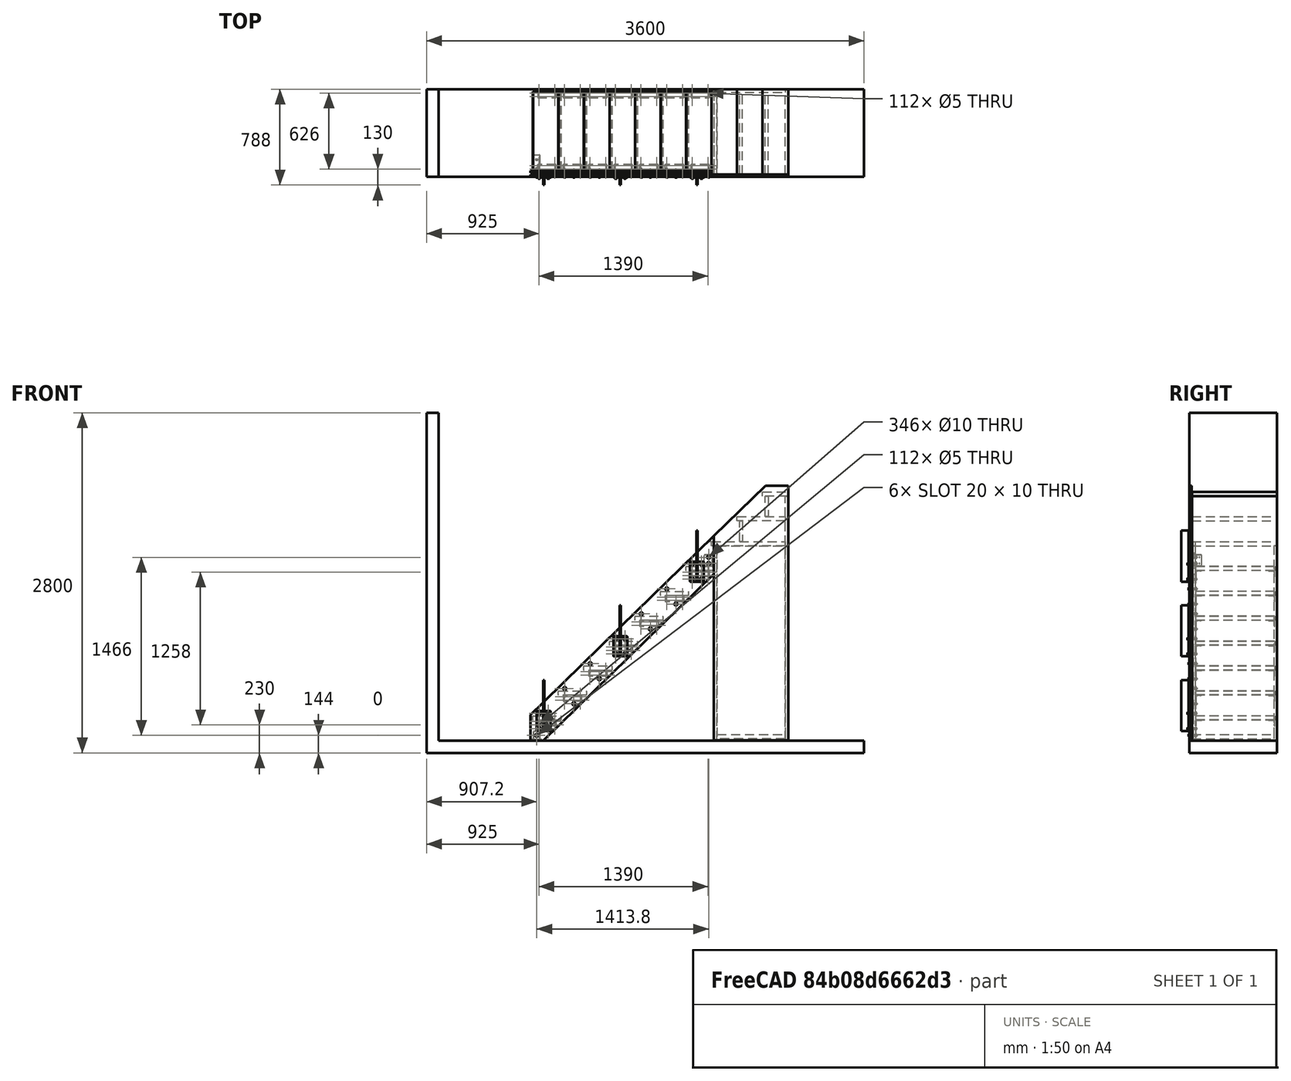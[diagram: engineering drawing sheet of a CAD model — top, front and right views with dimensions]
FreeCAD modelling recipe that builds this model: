
FCSTD DOCUMENT  (FreeCAD 0.17R10980 (Git))
Label: double_beam
License: All rights reserved
LicenseURL: http://en.wikipedia.org/wiki/All_rights_reserved
objects: Part::FeaturePython×27, Part::Part2DObjectPython×22, Part::Extrusion×12, Part::Compound×11, Part::Feature×9, Part::Cut×5, App::DocumentObjectGroupPython×2, App::DocumentObjectGroup×2
note: 86 computed .brp shape members not serialized (recipe doc carries the construction recipe); baked Part::Feature solids carry a one-line shape summary decoded from their .brp

FEATURE [Part::FeaturePython] beam_01  # a2plus imported part (geometry in sourceFile) (typed FeaturePython)
  fixedPosition = true
  sourceFile = beam.fcstd
  timeLastImport = 1.49397e+09
  updateColors = true
FEATURE [Part::FeaturePython] fridge_box_panels_01  # a2plus imported part (geometry in sourceFile) (typed FeaturePython)
  fixedPosition = false
  sourceFile = A711_fridge_box_panels.fcstd
  timeLastImport = 1.49389e+09
  updateColors = true
FEATURE [Part::Feature] fridge_box_panels_01_cs
  shape: bbox 630 x 3e-07 x 2050 mm, 0 faces, 0 solids (baked)
FEATURE [Part::Part2DObjectPython] DWire  # Draft 2D object (typed FeaturePython)
  ChamferSize = 0
  Closed = true
  End = (1515,-325,1605)
  FilletRadius = 0
  Length = 488.683
  MakeFace = true
  Points = (7) [(1490,-325,1605),(1470,-325,1605),(1470,-325,1640),(1423.45,-325,1640),(1423.45,-325,1757.79),(1515,-325,1757.79),(1515,-325,1605)]
  Start = (1490,-325,1605)
  Subdivisions = 0
  Support = -> [beam_01]
FEATURE [Part::FeaturePython] Clone  label="beam_004"  # Draft clone (typed FeaturePython)
  AttacherType = Attacher::AttachEngine3D
  Objects = -> [beam_01]
  Placement = pos=(0,-30,0) rot=(0,0,1;0rad)
  Scale = (1,1,1)
FEATURE [Part::FeaturePython] stair_profile_01  # a2plus imported part (geometry in sourceFile) (typed FeaturePython)
  fixedPosition = false
  sourceFile = stair_profile.fcstd
  timeLastImport = 1.4938e+09
  updateColors = true
FEATURE [Part::FeaturePython] step_01  # a2plus imported part (geometry in sourceFile) (typed FeaturePython)
  fixedPosition = false
  sourceFile = step.fcstd
  timeLastImport = 1.4938e+09
  updateColors = true
FEATURE [Part::FeaturePython] beam_plate_01  # a2plus imported part (geometry in sourceFile) (typed FeaturePython)
  fixedPosition = false
  sourceFile = beam_plate.fcstd
  timeLastImport = 1.49389e+09
  updateColors = true
FEATURE [Part::Feature] Union
  shape: bbox 26 x 2e-07 x 126 mm, 1 faces, 0 solids (baked)
FEATURE [Part::Feature] Union001
  shape: bbox 86 x 2e-07 x 26 mm, 1 faces, 0 solids (baked)
FEATURE [Part::Part2DObjectPython] Circle001  # Draft 2D object (typed FeaturePython)
  FirstAngle = 0
  LastAngle = 0
  MakeFace = true
  Placement = pos=(32.2,-325,44) rot=(-1,0,0;1.5708rad)
  Radius = 5
FEATURE [Part::Part2DObjectPython] Circle  # Draft 2D object (typed FeaturePython)
  FirstAngle = 0
  LastAngle = 0
  MakeFace = true
  Placement = pos=(1446,-325,1510) rot=(-1,0,0;1.5708rad)
  Radius = 5
FEATURE [Part::Part2DObjectPython] Circle002  # Draft 2D object (typed FeaturePython)
  FirstAngle = 0
  LastAngle = 0
  MakeFace = true
  Placement = pos=(1446,-325,1460) rot=(-1,0,0;1.5708rad)
  Radius = 5
FEATURE [Part::Compound] Compound001
  Links = -> [Union,Union001,DWire]
FEATURE [Part::Compound] Compound002
  Links = -> [Circle001,Circle,Circle002]
FEATURE [Part::Compound] Compound003
  Links = -> [Compound002,Compound001]
FEATURE [Part::Extrusion] Extrude
  Base = -> Compound003
  Dir = (0,-1,0)
  DirMode = 0
  FaceMakerClass = Part::FaceMakerBullseye
  LengthFwd = 20
  LengthRev = 0
  Solid = false
  Symmetric = false
FEATURE [Part::Cut] Cut
  Base = -> beam_01
  Tool = -> Extrude
FEATURE [Part::FeaturePython] Panel001  # WARN: FeaturePython — macro-defined, semantics opaque (R4)
  Area = 0
  Base = -> Cut
  FaceMaker = 0
  HorizontalArea = 0
  Length = 0
  MoveWithHost = false
  Normal = (0,0,0)
  PerimeterLength = 0
  Role = 0
  Sheets = 1
  Thickness = 10
  VerticalArea = 0
  WaveDirection = 0
  WaveHeight = 0
  WaveLength = 0
  WaveType = 0
  Width = 0
FEATURE [Part::Extrusion] Extrude001
  Base = -> Compound002
  Dir = (0,-1,0)
  DirMode = 0
  FaceMakerClass = Part::FaceMakerBullseye
  LengthFwd = 20
  LengthRev = 0
  Placement = pos=(0,-30,0) rot=(0,0,1;0rad)
  Solid = false
  Symmetric = false
FEATURE [Part::Cut] Cut001
  Base = -> Clone
  Tool = -> Extrude001
FEATURE [Part::FeaturePython] Panel  # WARN: FeaturePython — macro-defined, semantics opaque (R4)
  Area = 0
  Base = -> Cut001
  FaceMaker = 0
  HorizontalArea = 0
  Length = 0
  MoveWithHost = false
  Normal = (0,0,0)
  PerimeterLength = 0
  Role = 0
  Sheets = 1
  Thickness = 10
  VerticalArea = 0
  WaveDirection = 0
  WaveHeight = 0
  WaveLength = 0
  WaveType = 0
  Width = 0
FEATURE [Part::Part2DObjectPython] Circle003  # Draft 2D object (typed FeaturePython)
  FirstAngle = 0
  LastAngle = 0
  MakeFace = true
  Placement = pos=(32.2,-375,44) rot=(1,0,0;1.5708rad)
  Radius = 12.5
FEATURE [Part::Extrusion] Extrude002
  Base = -> Circle003
  Dir = (0,-1,0)
  DirMode = 0
  FaceMakerClass = Part::FaceMakerBullseye
  LengthFwd = 2
  LengthRev = 0
  Solid = false
  Symmetric = false
FEATURE [Part::Part2DObjectPython] Circle004  # Draft 2D object (typed FeaturePython)
  FirstAngle = 0
  LastAngle = 0
  MakeFace = true
  Placement = pos=(32.2,-375,44) rot=(1,0,0;1.5708rad)
  Radius = 5
FEATURE [Part::Extrusion] Extrude003
  Base = -> Circle004
  Dir = (0,-1,0)
  DirMode = 0
  FaceMakerClass = Part::FaceMakerBullseye
  LengthFwd = 2
  LengthRev = 0
  Solid = false
  Symmetric = false
FEATURE [Part::Cut] Cut002  label="washer"
  Base = -> Extrude002
  Tool = -> Extrude003
FEATURE [Part::Feature] BOLTS_part011_cs
  Placement = pos=(0,0,-2.5) rot=(0,0,1;0rad)
  shape: bbox 17 x 19.63 x 3e-07 mm, 0 faces, 0 solids (baked)
FEATURE [Part::Extrusion] Extrude004  label="nuts"
  Base = -> BOLTS_part011_cs
  Dir = (0,0,1)
  DirMode = 0
  FaceMakerClass = Part::FaceMakerBullseye
  LengthFwd = 6
  LengthRev = 0
  Placement = pos=(32.2,-347,44) rot=(1,0,0;1.5708rad)
  Solid = true
  Symmetric = false
FEATURE [Part::FeaturePython] Component001  label="washer002"  # WARN: FeaturePython — macro-defined, semantics opaque (R4)
  CloneOf = -> Cut002
  HorizontalArea = 0
  MoveWithHost = false
  PerimeterLength = 0
  Placement = pos=(0,30,0) rot=(0,0,1;0rad)
  Role = 0
  VerticalArea = 0
FEATURE [Part::FeaturePython] Component002  label="washer003"  # WARN: FeaturePython — macro-defined, semantics opaque (R4)
  CloneOf = -> Cut002
  HorizontalArea = 0
  MoveWithHost = false
  PerimeterLength = 0
  Placement = pos=(0,52,0) rot=(0,0,1;0rad)
  Role = 0
  VerticalArea = 0
FEATURE [Part::FeaturePython] Component003  label="nuts001"  # WARN: FeaturePython — macro-defined, semantics opaque (R4)
  CloneOf = -> Extrude004
  HorizontalArea = 0
  MoveWithHost = false
  PerimeterLength = 0
  Placement = pos=(32.2,-317,44) rot=(1,0,0;1.5708rad)
  Role = 0
  VerticalArea = 0
FEATURE [Part::Feature] BOLTS_part  label="Hexagon head bolt DIN 931 M10 - 66.0"
  Placement = pos=(32.2,-383.4,44) rot=(-1,0,0;1.5708rad)
  shape: bbox 17 x 72.4 x 19.63 mm, 11 faces (baked)
FEATURE [Part::Feature] step_01_cs  label="hd_steps_cs"
  shape: bbox 1490 x 3e-07 x 1265 mm, 0 faces, 0 solids (baked)
FEATURE [Part::FeaturePython] fridge_box_door_01  # a2plus imported part (geometry in sourceFile) (typed FeaturePython)
  Placement = pos=(0,1e-12,0) rot=(0,0,1;0rad)
  fixedPosition = false
  sourceFile = fridge_box_door.fcstd
  timeLastImport = 1.49385e+09
  updateColors = true
FEATURE [Part::Feature] fridge_box_door_01_cs
  shape: bbox 610 x 3e-07 x 2095 mm, 0 faces, 0 solids (baked)
FEATURE [Part::Part2DObjectPython] DWire003  # Draft 2D object (typed FeaturePython)
  ChamferSize = 0
  Closed = false
  End = (1490,-375,1605)
  FilletRadius = 0
  Length = 55
  MakeFace = true
  Points = (3) [(1470,-375,1640),(1470,-375,1605),(1490,-375,1605)]
  Start = (1470,-375,1640)
  Subdivisions = 0
FEATURE [Part::Part2DObjectPython] Line  # Draft 2D object (typed FeaturePython)
  ChamferSize = 0
  Closed = false
  End = (1490,-375,1640)
  FilletRadius = 0
  Length = 20
  MakeFace = true
  Points = (2) [(1470,-375,1640),(1490,-375,1640)]
  Start = (1470,-375,1640)
  Subdivisions = 0
FEATURE [Part::Part2DObjectPython] Line001  # Draft 2D object (typed FeaturePython)
  ChamferSize = 0
  Closed = false
  End = (1490,-375,0)
  FilletRadius = 0
  Length = 5
  MakeFace = true
  Points = (2) [(1490,-375,5),(1490,-375,0)]
  Start = (1490,-375,5)
  Subdivisions = 0
FEATURE [Part::Part2DObjectPython] Line002  # Draft 2D object (typed FeaturePython)
  ChamferSize = 0
  Closed = false
  End = (2100,-375,0)
  FilletRadius = 0
  Length = 5
  MakeFace = true
  Points = (2) [(2100,-375,5),(2100,-375,2.27374e-13)]
  Start = (2100,-375,5)
  Subdivisions = 0
FEATURE [Part::Part2DObjectPython] DWire001  # Draft 2D object (typed FeaturePython)
  ChamferSize = 0
  Closed = false
  End = (2725,-375,0)
  FilletRadius = 0
  Length = 6200
  MakeFace = true
  Points = (3) [(-775,-375,2700),(-775,-375,-1.13687e-13),(2725,-375,1.00626e-13)]
  Start = (-775,-375,2700)
  Subdivisions = 0
FEATURE [Part::Part2DObjectPython] DWire002  # Draft 2D object (typed FeaturePython)
  ChamferSize = 0
  Closed = false
  End = (2725,-375,2105)
  FilletRadius = 0
  Length = 1405
  MakeFace = true
  Points = (4) [(2725,-375,2260),(2100,-375,2260),(2100,-375,2105),(2725,-375,2105)]
  Start = (2725,-375,2260)
  Subdivisions = 0
FEATURE [Part::Compound] Compound007  label="07_section"
  Links = -> [DWire002,DWire001]
FEATURE [Part::FeaturePython] Component007  label="07_section002"  # WARN: FeaturePython — macro-defined, semantics opaque (R4)
  CloneOf = -> Compound007
  HorizontalArea = 0
  MoveWithHost = false
  PerimeterLength = 0
  Role = 0
  VerticalArea = 0
FEATURE [Part::FeaturePython] Component008  label="07_section003"  # WARN: FeaturePython — macro-defined, semantics opaque (R4)
  CloneOf = -> Compound007
  HorizontalArea = 0
  MoveWithHost = false
  PerimeterLength = 0
  Role = 0
  VerticalArea = 0
FEATURE [App::DocumentObjectGroupPython] VisGroup001  label="hd_steps"  # scripted group (container) (typed FeaturePython)
  Group = -> [step_01_cs,Component008]
FEATURE [Part::FeaturePython] Component009  label="07_section004"  # WARN: FeaturePython — macro-defined, semantics opaque (R4)
  CloneOf = -> Compound007
  HorizontalArea = 0
  MoveWithHost = false
  PerimeterLength = 0
  Role = 0
  VerticalArea = 0
FEATURE [Part::FeaturePython] railing_plate_01  # a2plus imported part (geometry in sourceFile) (typed FeaturePython)
  fixedPosition = false
  sourceFile = railing_plate.fcstd
  timeLastImport = 1.49397e+09
  updateColors = true
FEATURE [Part::Compound] Compound010  label="main"
  Links = -> [Panel,Panel001]
FEATURE [Part::Part2DObjectPython] Circle005  # Draft 2D object (typed FeaturePython)
  FirstAngle = 0
  LastAngle = 0
  MakeFace = true
  Placement = pos=(32.2,-375,44) rot=(1,0,0;1.5708rad)
  Radius = 12.5
FEATURE [Part::Extrusion] Extrude007
  Base = -> Circle005
  Dir = (0,-1,0)
  DirMode = 0
  FaceMakerClass = Part::FaceMakerBullseye
  LengthFwd = 2
  LengthRev = 0
  Solid = false
  Symmetric = false
FEATURE [Part::Part2DObjectPython] Circle006  # Draft 2D object (typed FeaturePython)
  FirstAngle = 0
  LastAngle = 0
  MakeFace = true
  Placement = pos=(32.2,-375,44) rot=(1,0,0;1.5708rad)
  Radius = 5
FEATURE [Part::Extrusion] Extrude008
  Base = -> Circle006
  Dir = (0,-1,0)
  DirMode = 0
  FaceMakerClass = Part::FaceMakerBullseye
  LengthFwd = 2
  LengthRev = 0
  Solid = false
  Symmetric = false
FEATURE [Part::Cut] Cut003  label="washer004"
  Base = -> Extrude007
  Placement = pos=(0,-8,0) rot=(0,0,1;0rad)
  Tool = -> Extrude008
FEATURE [Part::Feature] BOLTS_part011_cs001
  Placement = pos=(0,0,-2.5) rot=(0,0,1;0rad)
  shape: bbox 17 x 19.63 x 3e-07 mm, 0 faces, 0 solids (baked)
FEATURE [Part::Extrusion] Extrude009  label="nuts002"
  Base = -> BOLTS_part011_cs001
  Dir = (0,0,1)
  DirMode = 0
  FaceMakerClass = Part::FaceMakerBullseye
  LengthFwd = 6
  LengthRev = 0
  Placement = pos=(32.2,-347,44) rot=(1,0,0;1.5708rad)
  Solid = true
  Symmetric = false
FEATURE [Part::FeaturePython] Component011  label="washer006"  # WARN: FeaturePython — macro-defined, semantics opaque (R4)
  CloneOf = -> Cut003
  HorizontalArea = 0
  MoveWithHost = false
  PerimeterLength = 0
  Placement = pos=(0,30,0) rot=(0,0,1;0rad)
  Role = 0
  VerticalArea = 0
FEATURE [Part::FeaturePython] Component012  label="washer007"  # WARN: FeaturePython — macro-defined, semantics opaque (R4)
  CloneOf = -> Cut003
  HorizontalArea = 0
  MoveWithHost = false
  PerimeterLength = 0
  Placement = pos=(0,52,0) rot=(0,0,1;0rad)
  Role = 0
  VerticalArea = 0
FEATURE [Part::FeaturePython] Component013  label="nuts003"  # WARN: FeaturePython — macro-defined, semantics opaque (R4)
  CloneOf = -> Extrude009
  HorizontalArea = 0
  MoveWithHost = false
  PerimeterLength = 0
  Placement = pos=(32.2,-317,44) rot=(1,0,0;1.5708rad)
  Role = 0
  VerticalArea = 0
FEATURE [Part::Feature] BOLTS_part001  label="Hexagon head bolt DIN 931 M10 - 66.001"
  Placement = pos=(32.2,-391.4,44) rot=(-1,0,0;1.5708rad)
  shape: bbox 17 x 72.4 x 19.63 mm, 11 faces (baked)
FEATURE [Part::Part2DObjectPython] Circle009  # Draft 2D object (typed FeaturePython)
  FirstAngle = 0
  LastAngle = 0
  MakeFace = true
  Placement = pos=(32.2,-355,44) rot=(1,0,0;1.5708rad)
  Radius = 12.5
FEATURE [Part::Extrusion] Extrude013
  Base = -> Circle009
  Dir = (0,1,0)
  DirMode = 0
  FaceMakerClass = Part::FaceMakerBullseye
  LengthFwd = 2
  LengthRev = 0
  Solid = false
  Symmetric = false
FEATURE [Part::Part2DObjectPython] Circle010  # Draft 2D object (typed FeaturePython)
  FirstAngle = 0
  LastAngle = 0
  MakeFace = true
  Placement = pos=(32.2,-355,44) rot=(1,0,0;1.5708rad)
  Radius = 5
FEATURE [Part::Extrusion] Extrude014
  Base = -> Circle010
  Dir = (0,1,0)
  DirMode = 0
  FaceMakerClass = Part::FaceMakerBullseye
  LengthFwd = 2
  LengthRev = 0
  Solid = false
  Symmetric = false
FEATURE [Part::Cut] Cut005  label="washer012"
  Base = -> Extrude013
  Tool = -> Extrude014
FEATURE [Part::Compound] Compound004  label="fastener_and_nuts"
  Links = -> [Cut002,Extrude004,Component003,Component001,Component002,BOLTS_part,Cut005]
FEATURE [Part::FeaturePython] Component005  label="fastener_and_nuts002"  # WARN: FeaturePython — macro-defined, semantics opaque (R4)
  CloneOf = -> Compound004
  HorizontalArea = 0
  MoveWithHost = false
  PerimeterLength = 0
  Placement = pos=(1413.8,0,1466) rot=(0,0,1;0rad)
  Role = 0
  VerticalArea = 0
FEATURE [Part::FeaturePython] Component006  label="fastener_and_nuts003"  # WARN: FeaturePython — macro-defined, semantics opaque (R4)
  CloneOf = -> Compound004
  HorizontalArea = 0
  MoveWithHost = false
  PerimeterLength = 0
  Placement = pos=(1413.8,0,1416) rot=(0,0,1;0rad)
  Role = 0
  VerticalArea = 0
FEATURE [Part::Compound] Compound016  label="fasteners_and_nuts_unique"
  Links = -> [Component005,Compound004,Component006]
FEATURE [Part::FeaturePython] Component  label="washer013"  # WARN: FeaturePython — macro-defined, semantics opaque (R4)
  CloneOf = -> Cut005
  HorizontalArea = 0
  MoveWithHost = false
  PerimeterLength = 0
  Role = 0
  VerticalArea = 0
FEATURE [Part::Compound] Compound013  label="fastener_and_nuts_railing"
  Links = -> [Cut003,Extrude009,Component013,Component011,Component012,BOLTS_part001,Component]
  Placement = pos=(19.6902,0,56) rot=(0,0,1;0rad)
FEATURE [Part::FeaturePython] Component018  label="fastener_and_nuts006"  # WARN: FeaturePython — macro-defined, semantics opaque (R4)
  CloneOf = -> Compound004
  HorizontalArea = 0
  MoveWithHost = false
  PerimeterLength = 0
  Placement = pos=(229.7,0,386) rot=(0,0,1;0rad)
  Role = 0
  VerticalArea = 0
FEATURE [Part::FeaturePython] Array001  # Draft array (typed FeaturePython)
  Angle = 360
  ArrayType = 0
  Axis = (0,0,1)
  Base = -> Component018
  Center = (0,0,0)
  Fuse = false
  IntervalAxis = (0,0,0)
  IntervalX = (75,0,-125)
  IntervalY = (0,0,125)
  IntervalZ = (210,0,205)
  NumberPolar = 1
  NumberX = 2
  NumberY = 1
  NumberZ = 2
FEATURE [Part::FeaturePython] Array002  label="fasteners"  # Draft array (typed FeaturePython)
  Angle = 360
  ArrayType = 0
  Axis = (0,0,1)
  Base = -> Array001
  Center = (0,0,0)
  Fuse = false
  IntervalAxis = (0,0,0)
  IntervalX = (630,0,615)
  IntervalY = (0,1,0)
  IntervalZ = (0,0,0)
  NumberPolar = 1
  NumberX = 2
  NumberY = 1
  NumberZ = 1
FEATURE [Part::FeaturePython] Array  label="fasteners_railing"  # Draft array (typed FeaturePython)
  Angle = 360
  ArrayType = 0
  Axis = (0,0,1)
  Base = -> Compound013
  Center = (0,0,0)
  Fuse = false
  IntervalAxis = (0,0,0)
  IntervalX = (75,0,0)
  IntervalY = (0,0,125)
  IntervalZ = (630,0,615)
  NumberPolar = 1
  NumberX = 2
  NumberY = 2
  NumberZ = 3
FEATURE [Part::Part2DObjectPython] Rectangle  label="gr_detail001"  # Draft 2D object (typed FeaturePython)
  ChamferSize = 0
  Columns = 1
  FilletRadius = 10
  Height = 100
  Length = 100
  MakeFace = false
  Placement = pos=(216.28,-119.156,0) rot=(0,0,1;0rad)
  Rows = 1
FEATURE [Part::Part2DObjectPython] Rectangle001  # Draft 2D object (typed FeaturePython)
  ChamferSize = 0
  Columns = 1
  FilletRadius = 0
  Height = 1605
  Length = 700
  MakeFace = true
  Placement = pos=(1490,345,0) rot=(0.57735,-0.57735,-0.57735;2.0944rad)
  Rows = 1
  Support = -> [fridge_box_panels_01]
FEATURE [Part::Extrusion] Extrude015  label="fridge_box_side"
  Base = -> Rectangle001
  Dir = (1,0,0)
  DirMode = 0
  FaceMakerClass = Part::FaceMakerBullseye
  LengthFwd = 25
  LengthRev = 0
  Solid = false
  Symmetric = false
FEATURE [Part::Compound] Compound015  label="plan_detail"
  Links = -> [Panel,Panel001,railing_plate_01,beam_plate_01,Array002,Array,Compound016,Extrude015,fridge_box_door_01]
FEATURE [Part::Part2DObjectPython] Shape2DView  label="dr_railing_plate"  # Draft 2D object (typed FeaturePython)
  Base = -> railing_plate_01
  HiddenLines = false
  InPlace = true
  Placement = pos=(0,-375,2.64049e-05) rot=(0.57735,0.57735,-0.57735;2.0944rad)
  Projection = (0,-1,5.9605e-08)
  ProjectionMode = 0
  SegmentLength = 0.05
  Tessellation = false
FEATURE [Part::FeaturePython] plate_01  # a2plus imported part (geometry in sourceFile) (typed FeaturePython)
  fixedPosition = false
  sourceFile = plate.fcstd
  timeLastImport = 1.49399e+09
  updateColors = true
FEATURE [Part::Compound] Compound  label="main_view"
  Links = -> [Panel,Panel001,Component009,plate_01]
FEATURE [App::DocumentObjectGroup] Group  label="utilities"
  Group = -> [step_01,stair_profile_01,fridge_box_panels_01_cs,fridge_box_panels_01,beam_plate_01,fridge_box_door_01,plate_01]
FEATURE [Part::Part2DObjectPython] DWire004  # Draft 2D object (typed FeaturePython)
  ChamferSize = 0
  Closed = true
  End = (-875,-375,2700)
  FilletRadius = 0
  Length = 12800
  MakeFace = true
  Points = (6) [(-775,-375,2700),(-775,-375,-2.27374e-13),(2725,-375,2.27374e-13),(2725,-375,-100),(-875,-375,-100),(-875,-375,2700)]
  Start = (-775,-375,2700)
  Subdivisions = 0
  Support = -> [Compound]
FEATURE [Part::Extrusion] Extrude006  label="floor"
  Base = -> DWire004
  Dir = (0,1,0)
  DirMode = 0
  FaceMakerClass = Part::FaceMakerBullseye
  LengthFwd = 720
  LengthRev = 0
  Solid = false
  Symmetric = false
FEATURE [Part::Compound] Compound008  label="details"
  Links = -> [Panel,Panel001,fridge_box_panels_01,beam_plate_01,Extrude006,step_01,fridge_box_door_01,railing_plate_01,plate_01]
FEATURE [Part::Part2DObjectPython] Rectangle002  # Draft 2D object (typed FeaturePython)
  ChamferSize = 0
  Columns = 1
  FilletRadius = 5
  Height = 100
  Length = 150
  MakeFace = false
  Placement = pos=(-110,-375,290) rot=(1,0,0;1.5708rad)
  Rows = 1
  Support = -> [Compound010]
FEATURE [Part::Part2DObjectPython] Rectangle003  # Draft 2D object (typed FeaturePython)
  ChamferSize = 0
  Columns = 1
  FilletRadius = 5
  Height = 100
  Length = 150
  MakeFace = false
  Placement = pos=(105,-375,290) rot=(1,0,0;1.5708rad)
  Rows = 1
FEATURE [App::DocumentObjectGroupPython] VisGroup  label="013_fridge_box_and_railing"  # scripted group (container) (typed FeaturePython)
  Group = -> [fridge_box_door_01_cs,DWire003,Line001,Line,Line002,Component007,Shape2DView,Rectangle002,Rectangle003]
FEATURE [App::DocumentObjectGroup] Group001  label="drawing"
  Group = -> [Compound007,VisGroup,VisGroup001,Compound008,Compound,Compound015,Rectangle]
